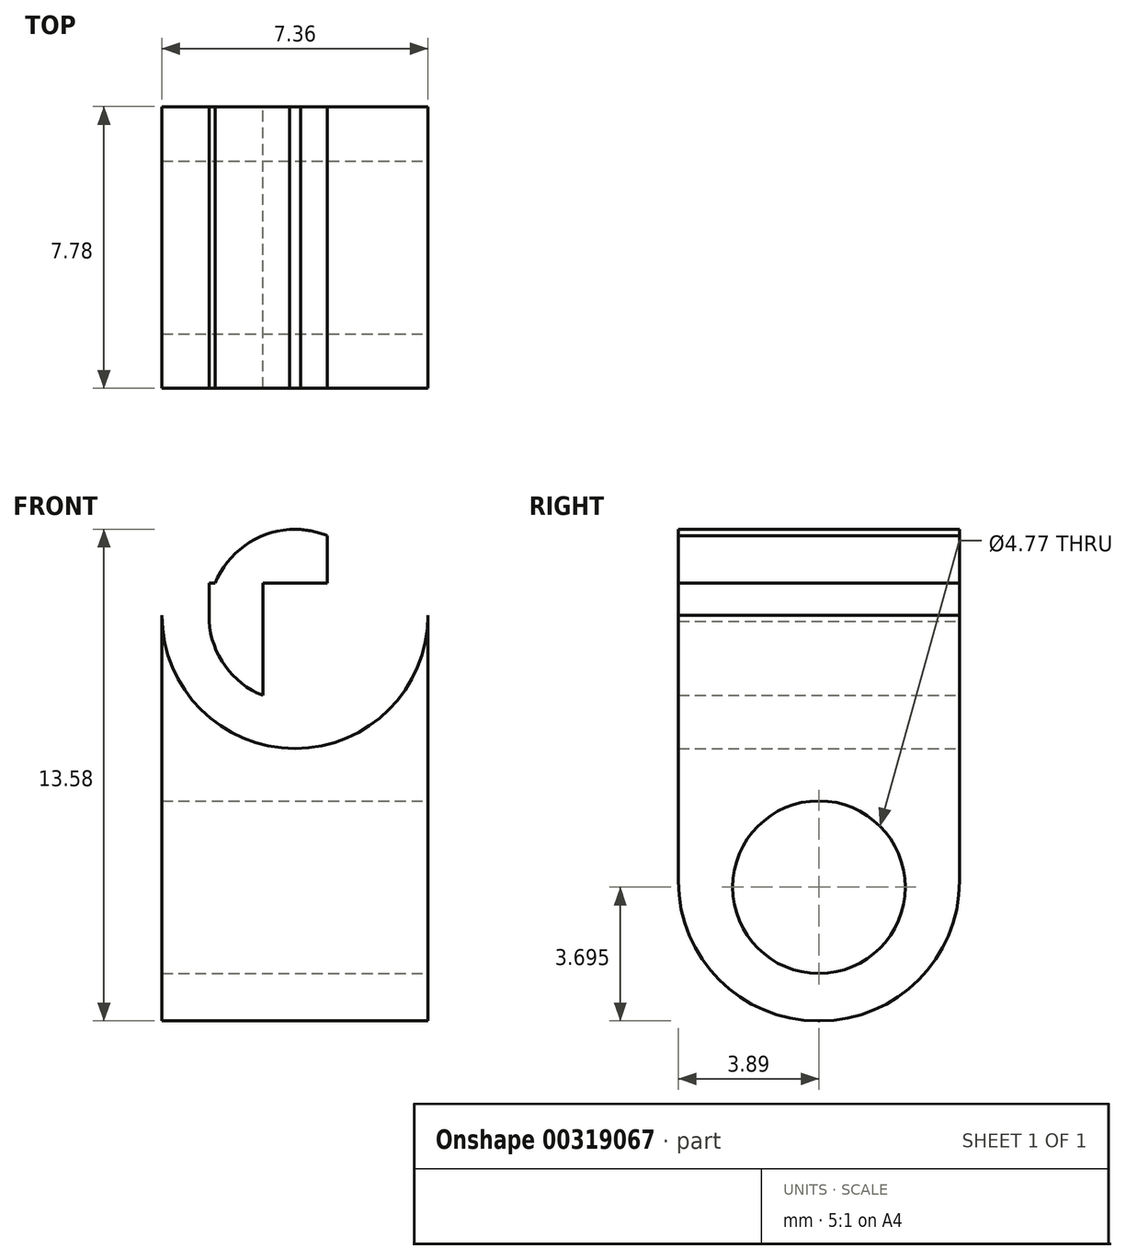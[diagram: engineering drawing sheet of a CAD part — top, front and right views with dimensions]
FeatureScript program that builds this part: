
annotation { "Feature Type Name" : "Feature", "Feature Type Description" : "" }
export const myFeature = defineFeature(function(context is Context, id is Id, definition is map)
    precondition{}
    {
        {
            var Q0;
            Q0=qCreatedBy(makeId("Front.planeOp"),FACE);
            var sketch = newSketch(context, id + "F0", { "sketchPlane" : qUnion([Q0])});
            skCircle(sketch, "E0", {"center": v(0, 0) * mm, "radius": 2.38 * mm});
            skCircle(sketch, "E1", {"center": v(0, 0) * mm, "radius": 3.67 * mm});
            skPoint(sketch, "E2", {"position": v(-3.68, 0) * mm});
            skPoint(sketch, "E3", {"position": v(0, -2.38) * mm});
            skLineSegment(sketch, "E4.bottom", {"start": v(-2.38, 0.9) * mm, "end": v(2.38, 0.9) * mm});
            skLineSegment(sketch, "E4.top", {"start": v(-2.38, -0.89) * mm, "end": v(2.38, -0.89) * mm});
            skLineSegment(sketch, "E4.left", {"start": v(-2.38, 0.89) * mm, "end": v(-2.38, -0.89) * mm});
            skLineSegment(sketch, "E4.right", {"start": v(2.38, 0.89) * mm, "end": v(2.38, -0.89) * mm});
            skLineSegment(sketch, "E5", {"start": v(0, 0.89) * mm, "end": v(0, -0.89) * mm});
            skLineSegment(sketch, "E6.bottom", {"start": v(-0.9, 2.38) * mm, "end": v(0.9, 2.38) * mm});
            skLineSegment(sketch, "E6.top", {"start": v(-0.9, -2.37) * mm, "end": v(0.9, -2.37) * mm});
            skLineSegment(sketch, "E6.left", {"start": v(-0.9, 2.37) * mm, "end": v(-0.9, -2.37) * mm});
            skLineSegment(sketch, "E6.right", {"start": v(0.89, 2.37) * mm, "end": v(0.89, -2.37) * mm});
            skLineSegment(sketch, "E7", {"start": v(-0.9, 0) * mm, "end": v(0.9, 0) * mm});
            skPoint(sketch, "E8", {"position": v(3.67, 0) * mm});
            skLineSegment(sketch, "E9", {"start": v(-3.68, 0) * mm, "end": v(-3.68, -11.2) * mm});
            skLineSegment(sketch, "E10", {"start": v(3.67, 0) * mm, "end": v(3.67, -11.2) * mm});
            skLineSegment(sketch, "E11", {"start": v(3.68, -11.2) * mm, "end": v(-3.67, -11.2) * mm});
            skSolve(sketch);
        }
        {
            var Q0;
            {var subQ3=sQuery(id+"F0.wireOp",EDGE,"E0");var subQ9=sQuery(id+"F0.wireOp",EDGE,"E4.bottom");var subQ13=makeQuery(id+"F0.imprint","INTERSECT",VERTEX,{"disambiguationData":[OD(0.0)],"derivedFrom":[subQ3,subQ9]});Q0=makeQuery(id+"F0.imprint","IMPRINT",FACE,{"disambiguationData":[TD([[makeQuery(id+"F0.imprint","IMPRINT",EDGE,{"disambiguationData":[TD([[subQ13,-1.0]])],"derivedFrom":subQ3}),-1.0]])]});}
            var Q1;
            {var subQ0=sQuery(id+"F0.wireOp",EDGE,"E9");Q1=makeQuery(id+"F0.imprint","IMPRINT",FACE,{"disambiguationData":[TD([[makeQuery(id+"F0.imprint","IMPRINT",EDGE,{"derivedFrom":subQ0}),1.0]])]});}
            var Q2;
            {var subQ0=sQuery(id+"F0.wireOp",EDGE,"E4.top");var subQ1=sQuery(id+"F0.wireOp",EDGE,"E0");var subQ2=makeQuery(id+"F0.imprint","INTERSECT",VERTEX,{"disambiguationData":[OD(0.0)],"derivedFrom":[subQ1,subQ0]});Q2=makeQuery(id+"F0.imprint","IMPRINT",FACE,{"disambiguationData":[TD([[makeQuery(id+"F0.imprint","IMPRINT",EDGE,{"disambiguationData":[TD([[subQ2,-1.0]])],"derivedFrom":subQ1}),1.0]])]});}
            var Q3;
            {var subQ0=sQuery(id+"F0.wireOp",EDGE,"E6.left");var subQ1=sQuery(id+"F0.wireOp",EDGE,"E0");var subQ2=makeQuery(id+"F0.imprint","INTERSECT",VERTEX,{"disambiguationData":[OD(0.0)],"derivedFrom":[subQ1,subQ0]});Q3=makeQuery(id+"F0.imprint","IMPRINT",FACE,{"disambiguationData":[TD([[makeQuery(id+"F0.imprint","IMPRINT",EDGE,{"disambiguationData":[TD([[subQ2,-1.0]])],"derivedFrom":subQ1}),1.0]])]});}
            var Q4;
            {var subQ0=sQuery(id+"F0.wireOp",EDGE,"E4.bottom");var subQ1=sQuery(id+"F0.wireOp",EDGE,"E0");var subQ2=makeQuery(id+"F0.imprint","INTERSECT",VERTEX,{"disambiguationData":[OD(0.0)],"derivedFrom":[subQ1,subQ0]});Q4=makeQuery(id+"F0.imprint","IMPRINT",FACE,{"disambiguationData":[TD([[makeQuery(id+"F0.imprint","IMPRINT",EDGE,{"disambiguationData":[TD([[subQ2,-1.0]])],"derivedFrom":subQ1}),1.0]])]});}
            var Q5;
            {var subQ0=sQuery(id+"F0.wireOp",EDGE,"E6.right");var subQ1=sQuery(id+"F0.wireOp",EDGE,"E0");var subQ2=makeQuery(id+"F0.imprint","INTERSECT",VERTEX,{"disambiguationData":[OD(1.0)],"derivedFrom":[subQ1,subQ0]});Q5=makeQuery(id+"F0.imprint","IMPRINT",FACE,{"disambiguationData":[TD([[makeQuery(id+"F0.imprint","IMPRINT",EDGE,{"disambiguationData":[TD([[subQ2,-1.0]])],"derivedFrom":subQ1}),1.0]])]});}
            extrude(context, id + "F1", {"entities" : qUnion([Q0, Q1, Q2, Q3, Q4, Q5]), "endBound" : BoundingType.SYMMETRIC, "depth" : 7.77 * mm});
        }
        {
            var Q0;
            Q0=makeQuery(id+"F1.opExtrude","SWEPT_FACE",FACE,{"disambiguationData":[OSD([sQuery(id+"F0.wireOp",EDGE,"E10")])]});
            var sketch = newSketch(context, id + "F2", { "sketchPlane" : qUnion([Q0])});
            skCircle(sketch, "E12", {"center": v(0, -7.5) * mm, "radius": 2.38 * mm});
            skPoint(sketch, "E13", {"position": v(0, -9.9) * mm});
            skSolve(sketch);
        }
        {
            var Q0;
            Q0=makeQuery(id+"F2.imprint","IMPRINT",FACE,{"disambiguationData":[TD([[makeQuery(id+"F2.imprint","IMPRINT",EDGE,{"derivedFrom":sQuery(id+"F2.wireOp",EDGE,"E12")}),1.0]])]});
            extrude(context, id + "F3", {"entities" : qUnion([Q0]), "operationType" : NewBodyOperationType.REMOVE, "endBound" : BoundingType.SYMMETRIC, "oppositeDirection" : true, "depth" : 25 * mm});
        }
        {
            var Q0;
            Q0=makeQuery(id+"F1.opExtrude","CAP_EDGE",EDGE,{"disambiguationData":[OSD([sQuery(id+"F0.wireOp",EDGE,"E11")])],"isStart":true});
            var Q1;
            Q1=makeQuery(id+"F1.opExtrude","CAP_EDGE",EDGE,{"disambiguationData":[OSD([sQuery(id+"F0.wireOp",EDGE,"E11")])],"isStart":false});
            fillet(context, id + "F4", {"entities" : qUnion([Q0, Q1]), "radius" : 3.86 * mm, "tangentPropagation" : true, "allowEdgeOverflow" : false});
        }
    });
